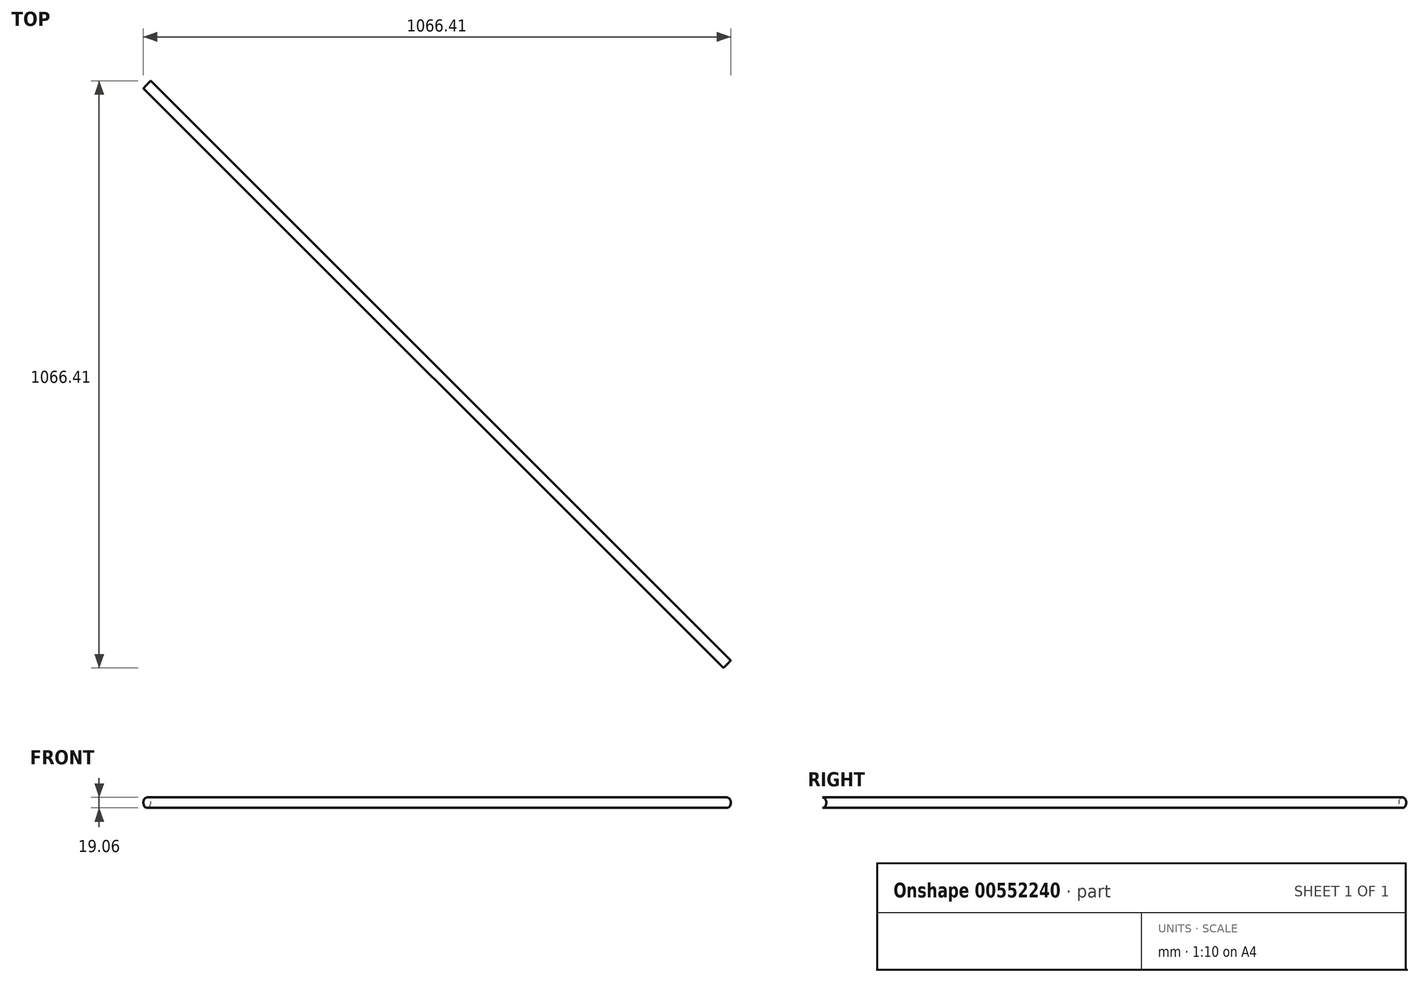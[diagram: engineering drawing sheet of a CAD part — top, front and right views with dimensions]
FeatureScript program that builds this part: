
annotation { "Feature Type Name" : "Feature", "Feature Type Description" : "" }
export const myFeature = defineFeature(function(context is Context, id is Id, definition is map)
    precondition{}
    {
        {
            var Q0;
            Q0=qCreatedBy(makeId("Front.planeOp"),FACE);
            var sketch = newSketch(context, id + "F0", { "sketchPlane" : qUnion([Q0])});
            skCircle(sketch, "E0", {"center": v(0, 0) * mm, "radius": 9.53 * mm});
            skSolve(sketch);
        }
        {
            var Q0;
            Q0=makeQuery(id+"F0.imprint","IMPRINT",FACE,{"disambiguationData":[TD([[makeQuery(id+"F0.imprint","IMPRINT",EDGE,{"derivedFrom":sQuery(id+"F0.wireOp",EDGE,"8IiYsvCz-TyMG-d5pM-uNmG-E6akeOXqpd7Q")}),1.0]])]});
            var Q1;
            Q1=makeQuery(id+"F0.imprint","IMPRINT",FACE,{"disambiguationData":[TD([[makeQuery(id+"F0.imprint","IMPRINT",EDGE,{"derivedFrom":sQuery(id+"F0.wireOp",EDGE,"E0")}),1.0]])]});
            extrude(context, id + "F1", {"entities" : qUnion([Q0, Q1]), "depth" : 1489.07 * mm, "offsetDistance" : 25.4 * mm});
        }
        {
            var Q0;
            Q0=qCreatedBy(makeId("Right.planeOp"),FACE);
            var sketch = newSketch(context, id + "F2", { "sketchPlane" : qUnion([Q0])});
            skLineSegment(sketch, "E1", {"start": v(0, 0) * mm, "end": v(0, 12.7) * mm});
            skSolve(sketch);
        }
        {
            var Q0;
            Q0=makeQuery(id+"F1.opExtrude","SWEPT_BODY",BODY,{"disambiguationData":[OSD([sQuery(id+"F0.wireOp",EDGE,"E0")])]});
            var Q1;
            Q1=sQuery(id+"F2.wireOp",EDGE,"E1");
            transform(context, id + "F3", {"entities" : qUnion([Q0]), "transformType" : TransformType.ROTATION, "transformAxis" : qUnion([Q1]), "angle" : 45 * degree, "makeCopy" : false});
        }
    });
